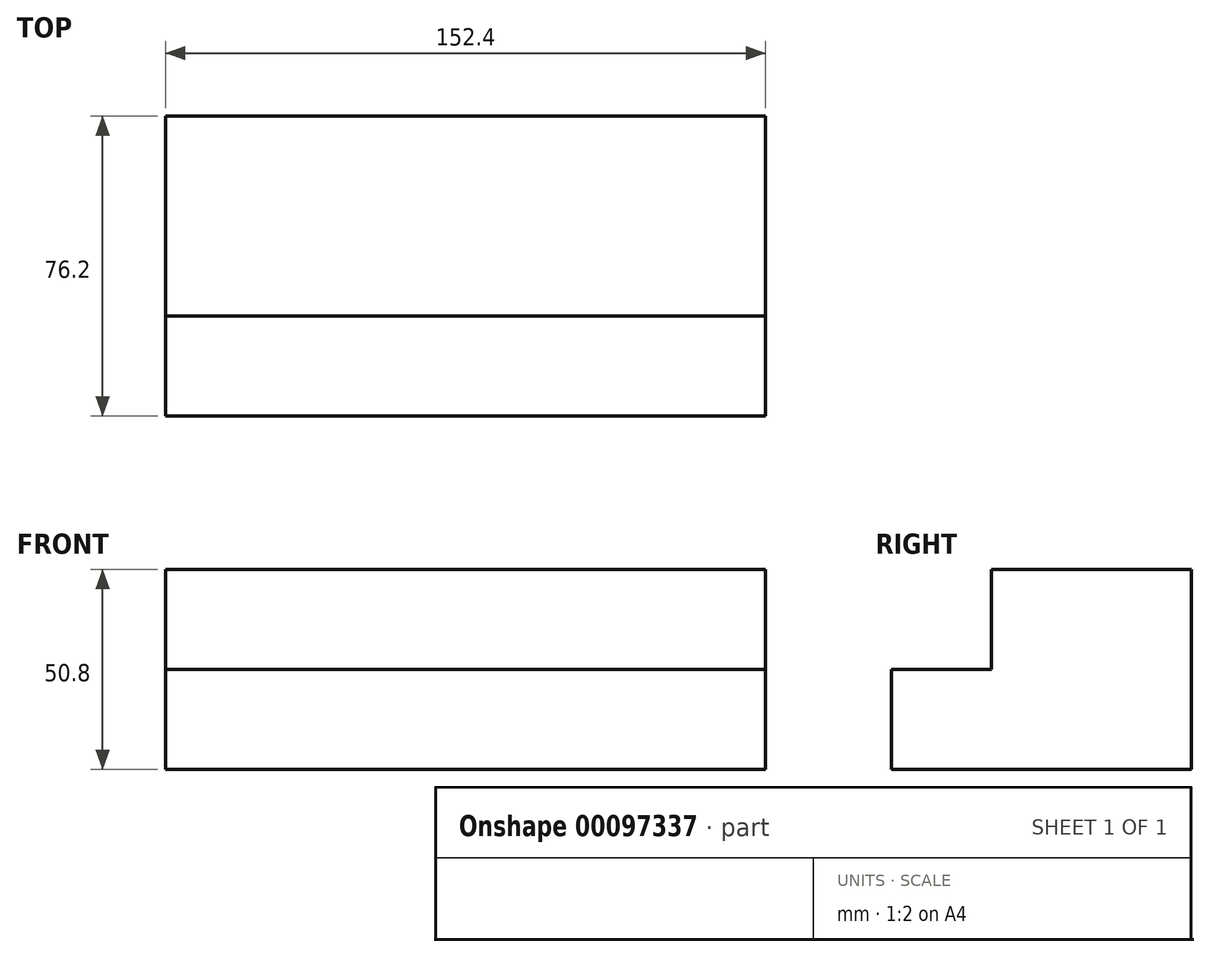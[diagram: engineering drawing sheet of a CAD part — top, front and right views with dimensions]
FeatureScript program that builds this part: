
annotation { "Feature Type Name" : "Feature", "Feature Type Description" : "" }
export const myFeature = defineFeature(function(context is Context, id is Id, definition is map)
    precondition{}
    {
        {
            var Q0;
            Q0=qCreatedBy(makeId("Right.planeOp"),FACE);
            var sketch = newSketch(context, id + "F0", { "sketchPlane" : qUnion([Q0])});
            skLineSegment(sketch, "E0", {"start": v(0, 0) * mm, "end": v(76.2, 0) * mm});
            skLineSegment(sketch, "E1", {"start": v(76.2, 0) * mm, "end": v(76.2, 50.8) * mm});
            skLineSegment(sketch, "E2", {"start": v(76.2, 50.8) * mm, "end": v(25.4, 50.8) * mm});
            skLineSegment(sketch, "E3", {"start": v(25.4, 50.8) * mm, "end": v(25.4, 25.4) * mm});
            skLineSegment(sketch, "E4", {"start": v(25.4, 25.4) * mm, "end": v(0, 25.4) * mm});
            skLineSegment(sketch, "E5", {"start": v(0, 25.4) * mm, "end": v(0, 0) * mm});
            skSolve(sketch);
        }
        {
            var Q0;
            Q0=makeQuery(id+"F0.imprint","IMPRINT",FACE,{"disambiguationData":[TD([[makeQuery(id+"F0.imprint","IMPRINT",EDGE,{"derivedFrom":sQuery(id+"F0.wireOp",EDGE,"E0")}),1.0]])]});
            extrude(context, id + "F1", {"entities" : qUnion([Q0]), "depth" : 152.4 * mm, "symmetric" : true});
        }
    });
